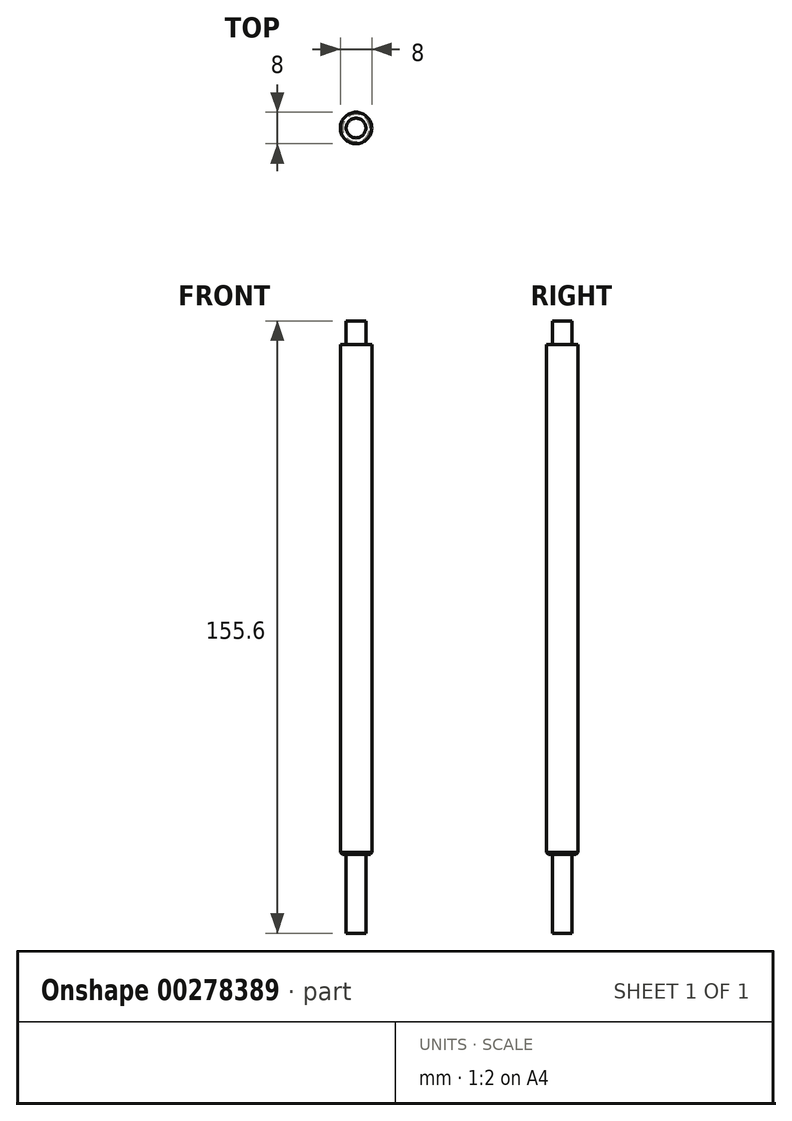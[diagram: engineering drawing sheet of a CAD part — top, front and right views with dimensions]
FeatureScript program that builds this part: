
annotation { "Feature Type Name" : "Feature", "Feature Type Description" : "" }
export const myFeature = defineFeature(function(context is Context, id is Id, definition is map)
    precondition{}
    {
        {
            var Q0;
            Q0=qCreatedBy(makeId("Top.planeOp"),FACE);
            var sketch = newSketch(context, id + "F0", { "sketchPlane" : qUnion([Q0])});
            skCircle(sketch, "E0", {"center": v(0, 0) * mm, "radius": 4 * mm});
            skSolve(sketch);
        }
        {
            var Q0;
            Q0 = qSketchRegion(id + "F0", true);
            extrude(context, id + "F1", {"entities" : qUnion([Q0]), "offsetDistance" : 25 * mm, "depth" : 155.6 * mm});
        }
        {
            var Q0;
            Q0=qCreatedBy(makeId("Top.planeOp"),FACE);
            var sketch = newSketch(context, id + "F2", { "sketchPlane" : qUnion([Q0])});
            skCircle(sketch, "E1", {"center": v(0, 0) * mm, "radius": 2.5 * mm});
            skCircle(sketch, "E2", {"center": v(0, 0) * mm, "radius": 6.5 * mm});
            skSolve(sketch);
        }
        {
            var Q0;
            Q0 = qSketchRegion(id + "F2", true);
            extrude(context, id + "F3", {"entities" : qUnion([Q0]), "operationType" : NewBodyOperationType.REMOVE, "offsetDistance" : 25 * mm, "depth" : 20 * mm});
        }
        {
            var Q0;
            Q0=makeQuery(id+"F1.opExtrude","CAP_FACE",FACE,{"disambiguationData":[OSD([sQuery(id+"F0.wireOp",EDGE,"E0")])],"isStart":false});
            var sketch = newSketch(context, id + "F4", { "sketchPlane" : qUnion([Q0])});
            skCircle(sketch, "E3", {"center": v(0, 0) * mm, "radius": 4 * mm});
            skCircle(sketch, "E4", {"center": v(0, 0) * mm, "radius": 2.5 * mm});
            skSolve(sketch);
        }
        {
            var Q0;
            Q0=makeQuery(id+"F4.imprint","IMPRINT",FACE,{"disambiguationData":[TD([[makeQuery(id+"F4.imprint","IMPRINT",EDGE,{"derivedFrom":sQuery(id+"F4.wireOp",EDGE,"E3")}),1.0]])]});
            var Q1;
            Q1=makeQuery(id+"F4.imprint","IMPRINT",FACE,{"disambiguationData":[TD([[makeQuery(id+"F4.imprint","IMPRINT",EDGE,{"derivedFrom":sQuery(id+"F4.wireOp",EDGE,"E4")}),-1.0]])]});
            var Q2;
            Q2=makeQuery(id+"F4.imprint","IMPRINT",FACE,{"disambiguationData":[TD([[makeQuery(id+"F4.imprint","IMPRINT",EDGE,{"derivedFrom":sQuery(id+"F4.wireOp",EDGE,"E3")}),1.0]])]});
            extrude(context, id + "F5", {"entities" : qUnion([Q0, Q1, Q2]), "operationType" : NewBodyOperationType.REMOVE, "oppositeDirection" : true, "depth" : 6 * mm, "offsetDistance" : 25 * mm});
        }
        {
            var Q0;
            Q0=makeQuery(id+"F3.boolean.opBoolean","COPY",EDGE,{"derivedFrom":makeQuery(id+"F3.opExtrude","CAP_EDGE",EDGE,{"disambiguationData":[OSD([sQuery(id+"F2.wireOp",EDGE,"E1")])],"isStart":true})});
            var Q1;
            Q1=makeQuery(id+"F3.boolean.opBoolean","INTERSECT",EDGE,{"derivedFrom":[makeQuery(id+"F1.opExtrude","SWEPT_FACE",FACE,{"disambiguationData":[OSD([sQuery(id+"F0.wireOp",EDGE,"E0")])]}),makeQuery(id+"F3.opExtrude","CAP_FACE",FACE,{"disambiguationData":[OSD([sQuery(id+"F2.wireOp",EDGE,"E1"),sQuery(id+"F2.wireOp",EDGE,"E2")])],"isStart":false})]});
            var Q2;
            Q2=makeQuery(id+"F5.boolean.opBoolean","COPY",EDGE,{"derivedFrom":makeQuery(id+"F5.opExtrude","CAP_EDGE",EDGE,{"disambiguationData":[OSD([sQuery(id+"F4.wireOp",EDGE,"E3")])],"isStart":false})});
            var Q3;
            Q3=makeQuery(id+"F5.boolean.opBoolean","COPY",EDGE,{"derivedFrom":makeQuery(id+"F5.opExtrude","CAP_EDGE",EDGE,{"disambiguationData":[OSD([sQuery(id+"F4.wireOp",EDGE,"E4")])],"isStart":true})});
            chamfer(context, id + "F6", {"entities" : qUnion([Q0, Q1, Q2, Q3]), "width" : 0.5 * mm, "tangentPropagation" : true});
        }
    });
